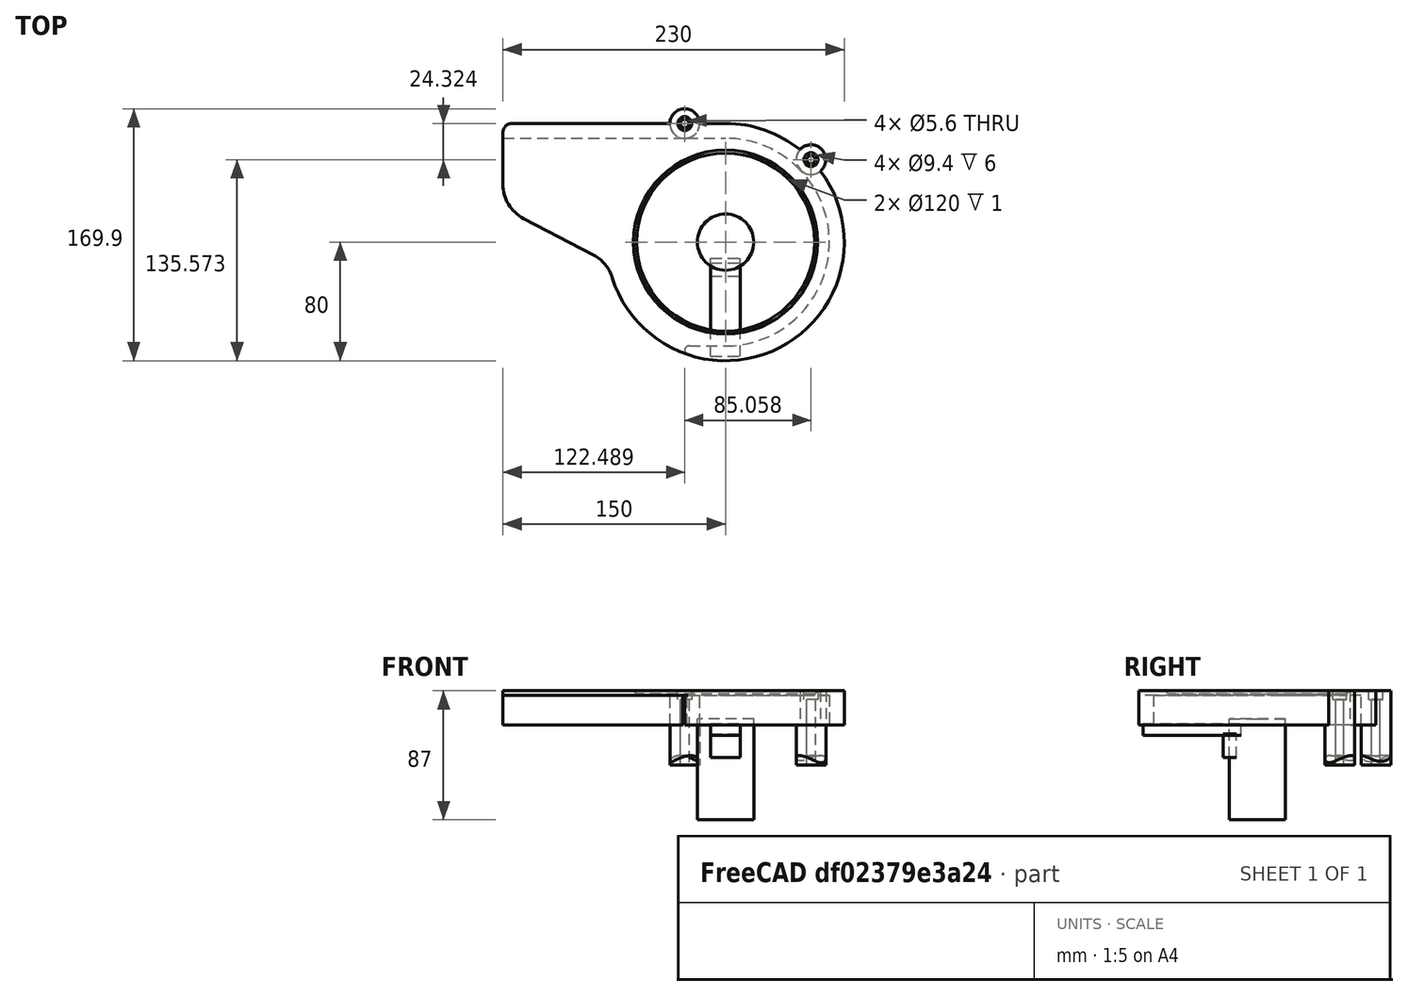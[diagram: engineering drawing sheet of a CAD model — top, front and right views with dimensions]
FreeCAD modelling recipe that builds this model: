
FCSTD DOCUMENT  (FreeCAD 0.19R)
Label: Changuard2
License: All rights reserved
LicenseURL: http://en.wikipedia.org/wiki/All_rights_reserved
objects: Sketcher::SketchObject×5, PartDesign::Pocket×3, PartDesign::Fillet×3, Part::Cylinder×3, PartDesign::Pad×2, Part::Cut×2, Part::Box×2, PartDesign::Chamfer×1, PartDesign::Body×1, Mesh::Feature×1
note: 31 computed .brp shape members not serialized (recipe doc carries the construction recipe); baked Part::Feature solids carry a one-line shape summary decoded from their .brp

FEATURE [Sketcher::SketchObject] Sketch
  FullyConstrained = false
  MapMode = 5
  Support = -> [XY_Plane]
  sketch-geometry (5):
    g0: Circle CenterX=0 CenterY=0 CenterZ=0 NormalX=0 NormalY=0 NormalZ=1 AngleXU=0 Radius=60
    g1: ArcOfCircle CenterX=0 CenterY=0 CenterZ=0 NormalX=0 NormalY=0 NormalZ=1 AngleXU=0 Radius=80 StartAngle=3.3175 EndAngle=7.85398
    g2: LineSegment StartX=-150 StartY=80 StartZ=0 EndX=2.84e-14 EndY=80 EndZ=0
    g3: LineSegment StartX=-150 StartY=80 StartZ=0 EndX=-150 EndY=23.2336 EndZ=0
    g4: LineSegment StartX=-150 StartY=23.2336 StartZ=0 EndX=-78.7655 EndY=-14 EndZ=0
  constraints (12):
    c: Coincident(g0,g-1)
    c: Coincident(g1,g0)
    c: Tangent(g2,g1) = 1.5708
    c: Horizontal(g2)
    c: Coincident(g3,g2)
    c: Vertical(g3)
    c: Coincident(g4,g3)
    c: Coincident(g4,g1)
    c: DistanceY(g1) = -14
    c: Distance(g2) = 150
    c: Radius(g1) = 80
    c: Radius(g0) = 60
FEATURE [PartDesign::Pad] Pad
  Direction = (1,1,1)
  Length = 23
  Length2 = 100
  Profile = -> Sketch
  Type = 0
FEATURE [Sketcher::SketchObject] Sketch001
  ExternalGeometry = -> [Pad]
  FullyConstrained = true
  MapMode = 5
  Placement = pos=(0,0,0) rot=(1,0,0;3.14159rad)
  Support = -> [Pad]
  sketch-geometry (4):
    g0: LineSegment StartX=-178.35 StartY=70 StartZ=0 EndX=2.84e-14 EndY=70 EndZ=0
    g1: ArcOfCircle CenterX=0 CenterY=0 CenterZ=0 NormalX=0 NormalY=0 NormalZ=1 AngleXU=0 Radius=70 StartAngle=4.71239 EndAngle=7.85398
    g2: LineSegment StartX=-178.35 StartY=-70 StartZ=0 EndX=0 EndY=-70 EndZ=0
    g3: LineSegment StartX=-178.35 StartY=70 StartZ=0 EndX=-178.35 EndY=-70 EndZ=0
  constraints (12):
    c: PointOnObject(g0,g-2)
    c: Horizontal(g0)
    c: Coincident(g1,g-1)
    c: Coincident(g1,g0)
    c: PointOnObject(g1,g-2)
    c: Coincident(g2,g1)
    c: Horizontal(g2)
    c: Coincident(g3,g0)
    c: Coincident(g3,g2)
    c: Vertical(g3)
    c: Distance(g0) = 178.35
    c: Distance(g-4,g1) = 10
FEATURE [PartDesign::Pocket] Pocket
  BaseFeature = -> Pad
  Length = 20
  Length2 = 100
  Profile = -> Sketch001
  Type = 0
FEATURE [Sketcher::SketchObject] Sketch002
  FullyConstrained = true
  MapMode = 5
  Placement = pos=(0,0,23) rot=(0,0,1;0rad)
  Support = -> [Pocket]
  sketch-geometry (5):
    g0: LineSegment StartX=-42.1643 StartY=122.454 StartZ=0 EndX=0 EndY=0 EndZ=0
    g1: LineSegment StartX=0 StartY=0 StartZ=0 EndX=111.699 EndY=107.867 EndZ=0
    g2: Circle CenterX=57.5472 CenterY=55.5727 CenterZ=0 NormalX=0 NormalY=0 NormalZ=1 AngleXU=0 Radius=10
    g3: Circle CenterX=-27.5105 CenterY=79.8963 CenterZ=0 NormalX=0 NormalY=0 NormalZ=1 AngleXU=0 Radius=10
    g4: Circle CenterX=0 CenterY=0 CenterZ=0 NormalX=0 NormalY=0 NormalZ=1 AngleXU=0 Radius=19
  constraints (14):
    c: Coincident(g0,g-1)
    c: Coincident(g1,g-1)
    c: Radius(g3) = 10
    c: Equal(g3,g2)
    c: PointOnObject(g3,g0)
    c: PointOnObject(g2,g1)
    c: Distance(g-1,g2) = 80
    c: Angle(g0) = -1.23918
    c: Distance(g1) = 155.28
    c: Distance(g0) = 129.51
    c: Radius(g4) = 19
    c: Coincident(g4,g-1)
    c: Distance(g-1,g3) = 84.5
    c: Angle(g1) = 0.767945
FEATURE [PartDesign::Pad] Pad001
  BaseFeature = -> Pocket
  Direction = (1,1,1)
  Length = 50
  Length2 = 100
  Profile = -> Sketch002
  Reversed = true
  Type = 0
FEATURE [Sketcher::SketchObject] Sketch005
  ExternalGeometry = -> [Pad001]
  FullyConstrained = false
  MapMode = 5
  Placement = pos=(0,0,23) rot=(0,0,1;0rad)
  Support = -> [Pad001]
  sketch-geometry (2):
    g0: Circle CenterX=-27.5105 CenterY=79.8963 CenterZ=0 NormalX=0 NormalY=0 NormalZ=1 AngleXU=0 Radius=2.8
    g1: Circle CenterX=57.5472 CenterY=55.5727 CenterZ=0 NormalX=0 NormalY=0 NormalZ=1 AngleXU=0 Radius=2.8
  constraints (2):
    c: Equal(g1,g0)
    c: Radius(g0) = 2.8
FEATURE [PartDesign::Pocket] Pocket001
  BaseFeature = -> Pad001
  Length = 5
  Length2 = 100
  Profile = -> Sketch005
  Type = 1
FEATURE [Sketcher::SketchObject] Sketch006
  ExternalGeometry = -> [Pocket001]
  FullyConstrained = true
  MapMode = 5
  Placement = pos=(0,0,23) rot=(0,0,1;0rad)
  Support = -> [Pocket001]
  sketch-geometry (2):
    g0: Circle CenterX=-27.5105 CenterY=79.8963 CenterZ=0 NormalX=0 NormalY=0 NormalZ=1 AngleXU=0 Radius=4.7
    g1: Circle CenterX=57.5472 CenterY=55.5727 CenterZ=0 NormalX=0 NormalY=0 NormalZ=1 AngleXU=0 Radius=4.7
  constraints (4):
    c: Radius(g1) = 4.7
    c: Equal(g1,g0)
    c: Coincident(g0,g-4)
    c: Coincident(g1,g-3)
FEATURE [PartDesign::Pocket] Pocket002
  BaseFeature = -> Pocket001
  Length = 6
  Length2 = 100
  Profile = -> Sketch006
  Type = 0
FEATURE [PartDesign::Fillet] Fillet
  Base = -> Pocket002 [Edge28,Edge5]
  BaseFeature = -> Pocket002
  Radius = 26
  SupportTransform = false
FEATURE [PartDesign::Chamfer] Chamfer
  Angle = 45
  Base = -> Fillet [Edge17]
  BaseFeature = -> Fillet
  ChamferType = 0
  FlipDirection = false
  Size = 2
  Size2 = 1
  SupportTransform = false
FEATURE [PartDesign::Fillet] Fillet001
  Base = -> Chamfer [Edge25]
  BaseFeature = -> Chamfer
  Radius = 6
  SupportTransform = false
FEATURE [PartDesign::Fillet] Fillet002
  Base = -> Fillet001 [Edge36]
  BaseFeature = -> Fillet001
  Radius = 3
  SupportTransform = false
FEATURE [PartDesign::Body] Body
  Group = -> [Sketch,Pad,Sketch001,Sketch002,Pocket,Pad001,Sketch005,Pocket001,Sketch006,Pocket002,Fillet,Chamfer,Fillet001,Fillet002]
  Origin = -> Origin
  Tip = -> Fillet002
FEATURE [Part::Cylinder] Cylinder  label="ST"
  Angle = 360
  AttacherType = Attacher::AttachEngine3D
  Height = 200
  Placement = pos=(-44,126,-35) rot=(0.939793,0.341743,0;1.5708rad)
  Radius = 14.3
FEATURE [Part::Cylinder] Cylinder001  label="DT"
  Angle = 360
  AttacherType = Attacher::AttachEngine3D
  Height = 200
  Placement = pos=(-16,-17,-35) rot=(-0.707107,0.707107,0;1.5708rad)
  Radius = 14.3
FEATURE [Part::Cut] Cut
  Base = -> Fillet002
  Tool = -> Cylinder
FEATURE [Part::Cut] Cut001
  Base = -> Cut
  Tool = -> Cylinder001
FEATURE [Mesh::Feature] Mesh  label="Cut001 (Meshed)"
FEATURE [Part::Cylinder] Cylinder002  label="Cylinder"
  Angle = 360
  AttacherType = Attacher::AttachEngine3D
  Height = 68
  Placement = pos=(0,0,-64) rot=(0,0,1;0rad)
  Radius = 19
FEATURE [Part::Box] Box  label="Cube"
  AttacherType = Attacher::AttachEngine3D
  Height = 8
  Length = 20
  Placement = pos=(-10,-77,-7) rot=(0,0,1;0rad)
  Width = 66
FEATURE [Part::Box] Box001  label="Cube001"
  AttacherType = Attacher::AttachEngine3D
  Height = 16
  Length = 20
  Placement = pos=(-10,-23,-22) rot=(0,0,1;0rad)
  Width = 9
